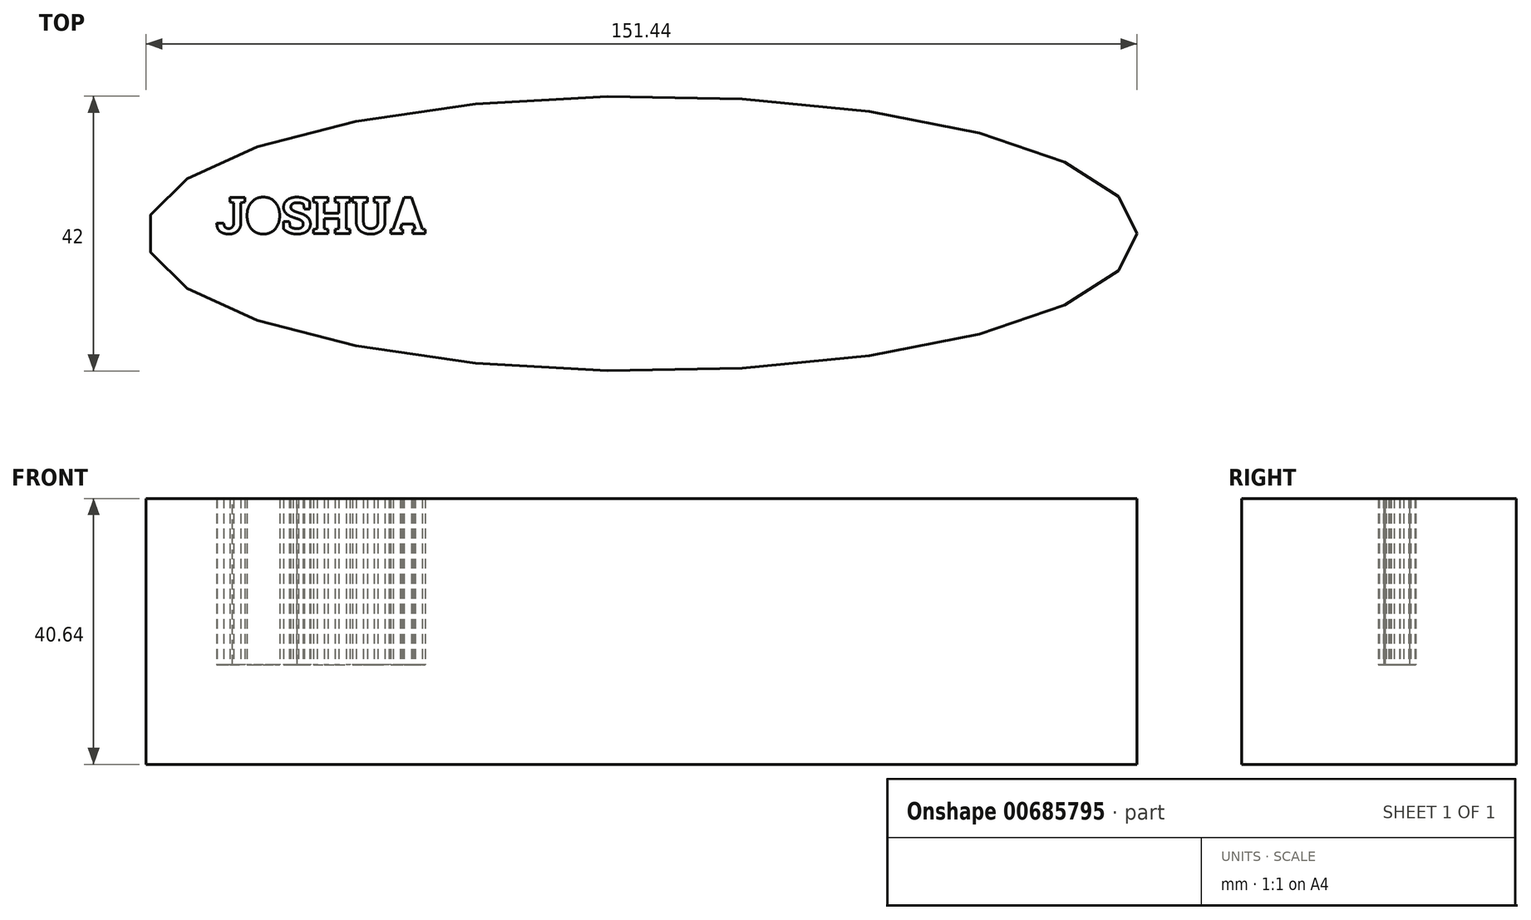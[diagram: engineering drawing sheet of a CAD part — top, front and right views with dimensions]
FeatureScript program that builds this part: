
annotation { "Feature Type Name" : "Feature", "Feature Type Description" : "" }
export const myFeature = defineFeature(function(context is Context, id is Id, definition is map)
    precondition{}
    {
        {
            var Q0;
            Q0=qCreatedBy(makeId("Top.planeOp"),FACE);
            var sketch = newSketch(context, id + "F0", { "sketchPlane" : qUnion([Q0])});
            skEllipse(sketch, "E0", {"center": v(-35.06, 0) * mm, "majorRadius": 75.72 * mm, "minorRadius": 21 * mm, "majorAxis": v(1, 0)});
            skSolve(sketch);
        }
        {
            var Q0;
            Q0=makeQuery(id+"F0.imprint","IMPRINT",FACE,{"disambiguationData":[TD([[makeQuery(id+"F0.imprint","IMPRINT",EDGE,{"derivedFrom":sQuery(id+"F0.wireOp",EDGE,"E0")}),1.0]])]});
            extrude(context, id + "F1", {"entities" : qUnion([Q0]), "depth" : 15.24 * mm, "offsetDistance" : 25.4 * mm});
        }
        {
            var Q0;
            Q0=makeQuery(id+"F1.opExtrude","CAP_FACE",FACE,{"disambiguationData":[OSD([sQuery(id+"F0.wireOp",EDGE,"E0")])],"isStart":false});
            var sketch = newSketch(context, id + "F2", { "sketchPlane" : qUnion([Q0])});
            skText(sketch, "E1", { "text": "JOSHUA", "fontName": "RobotoSlab-Bold.ttf"});
            const initialGuessF2  = {"E1": [-0.1001, 0, 1, 0, 0.00557]};
            skSetInitialGuess(sketch, initialGuessF2);
            skSolve(sketch);
        }
        {
            var Q0;
            Q0=makeQuery(id+"F2.imprint","IMPRINT",FACE,{"disambiguationData":[TD([[makeQuery(id+"F2.imprint","IMPRINT",EDGE,{"derivedFrom":sQuery(id+"F2.wireOp",EDGE,"E1.sketch_text.stroke-0")}),1.0]])]});
            var Q1;
            Q1 = qSketchRegion(id + "F2Cs5rFlcns4h1A_1", true);
            extrude(context, id + "F3", {"entities" : qUnion([Q0, Q1]), "operationType" : NewBodyOperationType.ADD, "depth" : 25.4 * mm, "offsetDistance" : 25.4 * mm});
        }
    });
